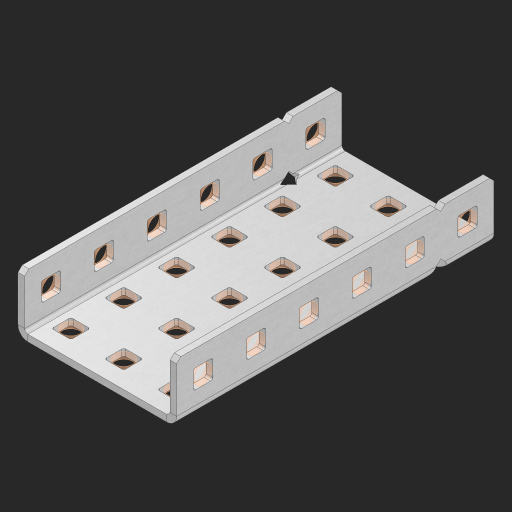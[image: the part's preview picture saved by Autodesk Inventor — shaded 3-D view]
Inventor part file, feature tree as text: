
AUTODESK INVENTOR PART (.ipt)
format: ipt  version: 2023 (Build 270158000, 158)  size: 747,520 bytes
history: native  units: in
note: dims shown in document units (in); Inventor stores cm internally (conversion verified against a paired STEP export)
features: other x35, extrude x29, sheet_metal_op x10, sketch x8, mirror x1, pattern_linear x1, chamfer x1
ambient origin geometry x8: Origin, YZ Plane, XZ Plane, XY Plane, X Axis, Y Axis, Z Axis, Center Point
bodies: Solid1 (feature_tree), Body (feature_tree)
feature tree (85):
  other  "Flange Pattern Plane"
  sheet_metal_op  "Flange Pattern"
  sheet_metal_op  "Body Pattern"
  other  "Arc Length"
  mirror  "Notch Mirror"
  pattern_linear  "Notch Pattern"  Spacing1=0.25in  [1 undecoded]
  chamfer  "End Chamfer"
  extrude  "Half Cut"  Depth=0.0625in
  sketch  "Sketch1"  dims[d0=1.5in]
  other  "Plate1"
  sketch  "Sketch2"  dims[d1=3.0in]
  other  "Plate2"
  sheet_metal_op  "Bend1"
  sheet_metal_op  "Corner1"
  sketch  "Sketch3"  dims[d2=0.0625in]
  other  "Flange Pattern Sketch"
  sketch  "Sketch7"  dims[d3=0.0625in]
  other  "Srf1"
  other  "Srf2"
  sketch  "Sketch8"  dims[d4=0.0312in]
  sketch  "Sketch9"  dims[d5=0.125in]
  other  "Srf91"
  sheet_metal_op  "Body Pattern Sketch"
  other  "Srf92"
  sketch  "Sketch13"  dims[d6=0.0625in]
  sketch  "Sketch14"  dims[d7=0.5in d8=90.0deg d9=0.0312in d10=0.25in d11=0.0625in d12=0.0625in d16=0.182in d17=0.02in d18=0.0625in d19=0.0in d20=0.25in d21=0.25in d46=0.172in d47=1.0in d48=0.0in d49=0.182in d50=0.02in d51=0.25in d52=0.25in d53=0.0625in d54=0.0in d55=0.172in d56=1.0in d57=0.0in d60=2.3622in d62=0.5in d63=1.1811in d65=0.5in d85=0.1473in d86=0.1782in d88=0.04in d89=0.0625in d90=0.0in d91=0.04in d92=0.0491in d95=2.5in d96=0.04in d97=0.25in d98=45.0deg d101=0.0in d102=2.497in d131=1.5in d132=2.3622in d134=0.5in d139=0.5in]
  other  "Srf856"
  other  "Srf1310"
  other  "Srf1311"
  other  "Srf1312"
  other  "Srf1376"
  other  "Srf1377"
  other  "Srf1728"
  other  "Srf1755"
  other  "Srf1878"
  other  "Srf1879"
  other  "Srf1880"
  other  "Srf1881"
  other  "Srf1882"
  other  "Srf1883"
  other  "Srf1942"
  other  "Srf1943"
  other  "Srf1944"
  other  "Srf1945"
  other  "Srf1946"
  other  "Srf1947"
  other  "Srf1948"
  other  "Srf1949"
  other  "Srf1950"
  other  "Srf1951"
  other  "Srf1952"
  other  "Srf1953"
  sheet_metal_op  "Flange Stamp"
  sheet_metal_op  "Flange Circle"
  sheet_metal_op  "Body Stamp"
  sheet_metal_op  "Body Circle"
  sheet_metal_op  "Notch"
  extrude  "ExtrusionSrf2"  Depth=0.0625in
  extrude  "ExtrusionSrf92"  Depth=1.5in
  extrude  "ExtrusionSrf856"  Depth=0.02in
  extrude  "ExtrusionSrf1310"  Depth=0.0625in
  extrude  "ExtrusionSrf1311"  TaperAngle=0.0deg  [1 undecoded]
  extrude  "ExtrusionSrf1312"  Depth=0.25in
  extrude  "ExtrusionSrf1376"  Depth=0.25in
  extrude  "ExtrusionSrf1377"  Depth=1.5in
  extrude  "ExtrusionSrf1728"  Depth=1.5in TaperAngle=0.0deg
  extrude  "ExtrusionSrf1755"  Depth=1.5in
  extrude  "ExtrusionSrf1878"  Depth=0.02in
  extrude  "ExtrusionSrf1879"  Depth=0.25in
  extrude  "ExtrusionSrf1880"  Depth=0.25in
  extrude  "ExtrusionSrf1881"  Depth=0.0625in
  extrude  "ExtrusionSrf1882"  TaperAngle=0.0deg  [1 undecoded]
  extrude  "ExtrusionSrf1883"  Depth=1.5in
  extrude  "ExtrusionSrf1942"  Depth=1.5in TaperAngle=0.0deg
  extrude  "ExtrusionSrf1943"  Depth=1.5in
  extrude  "ExtrusionSrf1944"  Depth=1.5in
  extrude  "ExtrusionSrf1945"  Depth=1.5in
  extrude  "ExtrusionSrf1946"  Depth=1.5in
  extrude  "ExtrusionSrf1947"  Depth=1.5in
  extrude  "ExtrusionSrf1948"  Depth=0.0625in
  extrude  "ExtrusionSrf1949"  TaperAngle=0.0deg  [1 undecoded]
  extrude  "ExtrusionSrf1950"  Depth=1.5in
  extrude  "ExtrusionSrf1951"  Depth=1.5in
  extrude  "ExtrusionSrf1952"  Depth=1.5in
  extrude  "ExtrusionSrf1953"  Depth=0.25in TaperAngle=45.0deg
note: 4 required parameter values undecoded (feature->parameter linkage not recoverable at this tier; creation-order binding heuristic only, values carry confidence <= 0.55)
